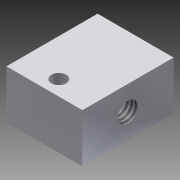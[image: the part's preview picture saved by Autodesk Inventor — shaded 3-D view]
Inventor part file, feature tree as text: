
AUTODESK INVENTOR PART (.ipt)
format: ipt  version: 2015 SP1 (Build 190203100, 203)  size: 91,136 bytes
history: native  units: in
note: dims shown in document units (in); Inventor stores cm internally (conversion verified against a paired STEP export)
features: hole x2, extrude x1, sketch x1
ambient origin geometry x8: Origin, YZ Plane, XZ Plane, XY Plane, X Axis, Y Axis, Z Axis, Center Point
bodies: Solid1 (feature_tree)
feature tree (4):
  extrude  "Extrusion1"  [1 undecoded]
  hole  "Hole1"  [1 undecoded]
  hole  "Hole2"  [1 undecoded]
  sketch  "Sketch1"  dims[d2=0.0in d3=0.0984in d4=0.2411in d5=0.0968in d6=0.2362in d7=0.1575in d8=0.0787in d9=90.0deg d10=0.315in d11=0.8108in d12=0.2953in d13=0.1575in d14=0.1276in d15=0.315in d16=0.1575in d17=0.0787in d18=90.0deg d19=0.4646in d20=0.8108in]
note: 3 required parameter values undecoded (feature->parameter linkage not recoverable at this tier; creation-order binding heuristic only, values carry confidence <= 0.55)
